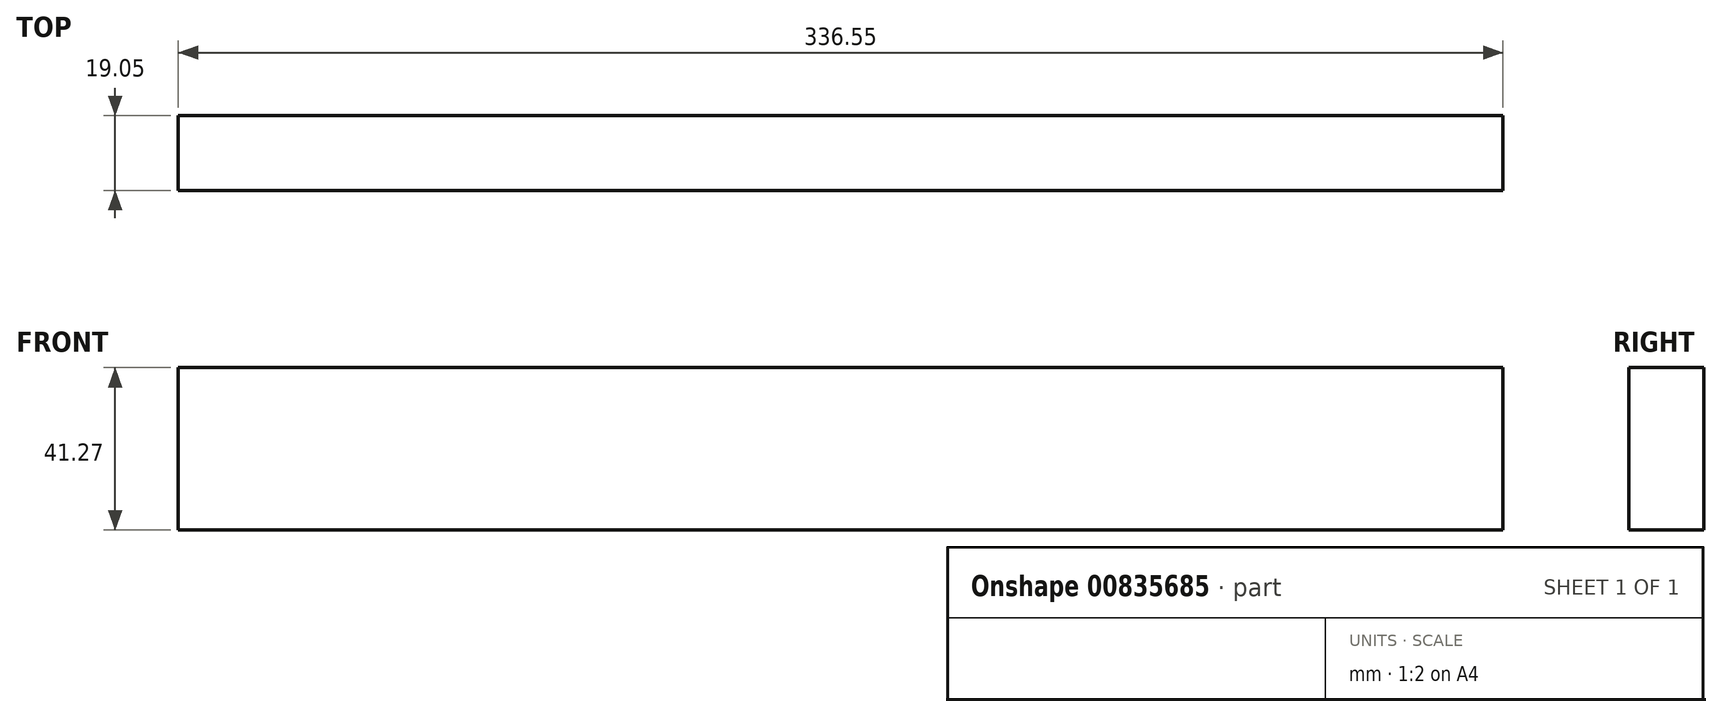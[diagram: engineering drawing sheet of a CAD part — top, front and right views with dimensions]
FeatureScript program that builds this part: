
annotation { "Feature Type Name" : "Feature", "Feature Type Description" : "" }
export const myFeature = defineFeature(function(context is Context, id is Id, definition is map)
    precondition{}
    {
        {
            var Q0;
            Q0=qCreatedBy(makeId("Front.planeOp"),FACE);
            var sketch = newSketch(context, id + "F0", { "sketchPlane" : qUnion([Q0])});
            skLineSegment(sketch, "E0.bottom", {"start": v(0, 0) * mm, "end": v(336.55, 0) * mm});
            skLineSegment(sketch, "E0.top", {"start": v(0, 41.28) * mm, "end": v(336.55, 41.28) * mm});
            skLineSegment(sketch, "E0.left", {"start": v(0, 0) * mm, "end": v(0, 41.28) * mm});
            skLineSegment(sketch, "E0.right", {"start": v(336.55, 0) * mm, "end": v(336.55, 41.28) * mm});
            skSolve(sketch);
        }
        {
            var Q0;
            Q0=qSketchRegion(id+"F0",true);
            extrude(context, id + "F1", {"entities" : qUnion([Q0]), "depth" : 19.05 * mm, "offsetDistance" : 25.4 * mm});
        }
    });
